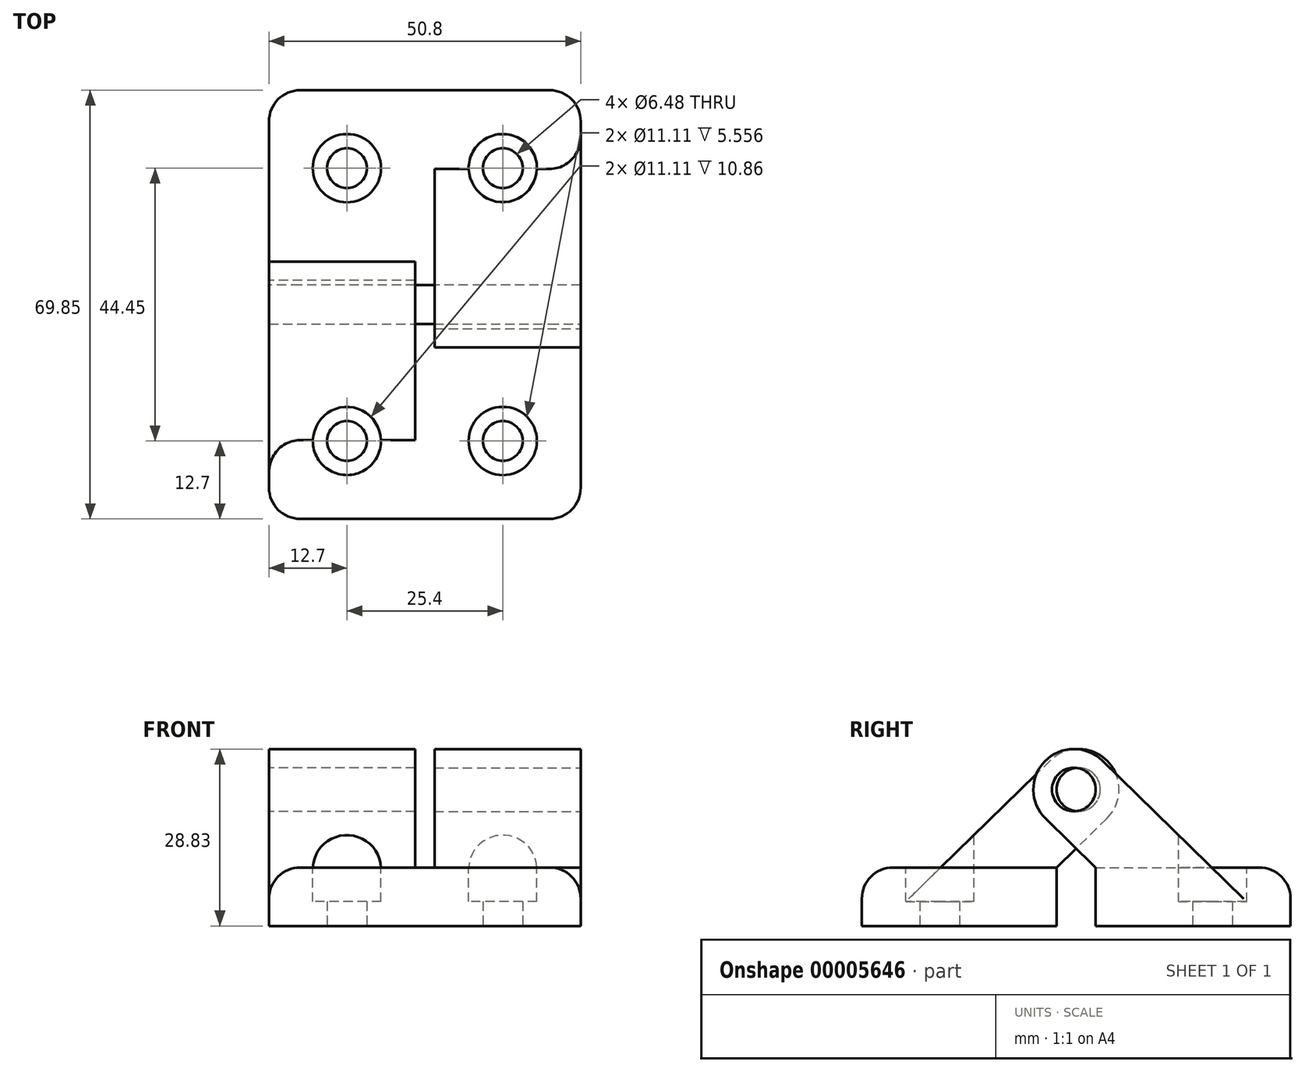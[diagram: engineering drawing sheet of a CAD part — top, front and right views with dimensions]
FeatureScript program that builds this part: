
annotation { "Feature Type Name" : "Feature", "Feature Type Description" : "" }
export const myFeature = defineFeature(function(context is Context, id is Id, definition is map)
    precondition{}
    {
        {
            var Q0;
            Q0=qCreatedBy(makeId("Top.planeOp"),FACE);
            var sketch = newSketch(context, id + "F0", { "sketchPlane" : qUnion([Q0])});
            skLineSegment(sketch, "E0.bottom", {"start": v(0, 0) * mm, "end": v(-50.8, 0) * mm});
            skLineSegment(sketch, "E0.top", {"start": v(0, 31.75) * mm, "end": v(-50.8, 31.75) * mm});
            skLineSegment(sketch, "E0.left", {"start": v(0, 0) * mm, "end": v(0, 31.75) * mm});
            skLineSegment(sketch, "E0.right", {"start": v(-50.8, 0) * mm, "end": v(-50.8, 31.75) * mm});
            skSolve(sketch);
        }
        {
            var Q0;
            Q0=makeQuery(id+"F0.imprint","IMPRINT",FACE,{"disambiguationData":[TD([[makeQuery(id+"F0.imprint","IMPRINT",EDGE,{"derivedFrom":sQuery(id+"F0.wireOp",EDGE,"E0.bottom")}),-1.0]])]});
            extrude(context, id + "F1", {"entities" : qUnion([Q0]), "depth" : 9.52 * mm});
        }
        {
            var Q0;
            Q0=makeQuery(id+"F1.opExtrude","SWEPT_FACE",FACE,{"disambiguationData":[OSD([sQuery(id+"F0.wireOp",EDGE,"E0.left")])]});
            var sketch = newSketch(context, id + "F2", { "sketchPlane" : qUnion([Q0])});
            skCircle(sketch, "E1", {"center": v(-3.56, 22.23) * mm, "radius": 3.56 * mm});
            skCircle(sketch, "E2", {"center": v(-3.56, 22.23) * mm, "radius": 6.6 * mm});
            skLineSegment(sketch, "E3", {"start": v(-8.17, 17.5) * mm, "end": v(0, 9.52) * mm});
            skLineSegment(sketch, "E4", {"start": v(1.06, 26.95) * mm, "end": v(18.9, 9.52) * mm});
            skSolve(sketch);
        }
        {
            var Q0;
            Q0 = qSketchRegion(id + "F2", true);
            var Q1;
            {var subQ3=sQuery(id+"F2.wireOp",EDGE,"E3");Q1=makeQuery(id+"F2.imprint","IMPRINT",FACE,{"disambiguationData":[TD([[makeQuery(id+"F2.imprint","IMPRINT",EDGE,{"derivedFrom":subQ3}),1.0]])]});}
            extrude(context, id + "F3", {"entities" : qUnion([Q0, Q1]), "operationType" : NewBodyOperationType.ADD, "oppositeDirection" : true, "depth" : 23.8 * mm});
        }
        {
            var Q0;
            Q0=makeQuery(id+"F1.opExtrude","CAP_FACE",FACE,{"disambiguationData":[OSD([sQuery(id+"F0.wireOp",EDGE,"E0.bottom"),sQuery(id+"F0.wireOp",EDGE,"E0.top"),sQuery(id+"F0.wireOp",EDGE,"E0.left"),sQuery(id+"F0.wireOp",EDGE,"E0.right")])],"isStart":true});
            var sketch = newSketch(context, id + "F4", { "sketchPlane" : qUnion([Q0])});
            skCircle(sketch, "E5", {"center": v(-12.7, -19.05) * mm, "radius": 3.24 * mm});
            skCircle(sketch, "E6", {"center": v(-38.1, -19.05) * mm, "radius": 3.24 * mm});
            skSolve(sketch);
        }
        {
            var Q0;
            Q0 = qSketchRegion(id + "F4", true);
            extrude(context, id + "F5", {"entities" : qUnion([Q0]), "operationType" : NewBodyOperationType.REMOVE, "oppositeDirection" : true, "depth" : 25.4 * mm});
        }
        {
            var Q0;
            Q0=makeQuery(id+"F1.opExtrude","CAP_FACE",FACE,{"disambiguationData":[OSD([sQuery(id+"F0.wireOp",EDGE,"E0.bottom"),sQuery(id+"F0.wireOp",EDGE,"E0.top"),sQuery(id+"F0.wireOp",EDGE,"E0.left"),sQuery(id+"F0.wireOp",EDGE,"E0.right")])],"isStart":false});
            var sketch = newSketch(context, id + "F6", { "sketchPlane" : qUnion([Q0])});
            skCircle(sketch, "E7.0", {"center": v(-38.1, 19.05) * mm, "radius": 3.24 * mm});
            skCircle(sketch, "E7.1", {"center": v(-12.7, 19.05) * mm, "radius": 3.24 * mm});
            skCircle(sketch, "E8", {"center": v(-38.1, 19.05) * mm, "radius": 5.56 * mm});
            skCircle(sketch, "E9", {"center": v(-12.7, 19.05) * mm, "radius": 5.56 * mm});
            skSolve(sketch);
        }
        {
            var Q0;
            Q0 = qSketchRegion(id + "F6", true);
            extrude(context, id + "F7", {"entities" : qUnion([Q0]), "operationType" : NewBodyOperationType.REMOVE, "oppositeDirection" : true, "depth" : 5.56 * mm});
        }
        {
            var Q0;
            Q0=makeQuery(id+"F6.imprint","IMPRINT",FACE,{"disambiguationData":[TD([[makeQuery(id+"F6.imprint","IMPRINT",EDGE,{"derivedFrom":sQuery(id+"F6.wireOp",EDGE,"E7.1")}),-1.0]])]});
            extrude(context, id + "F8", {"entities" : qUnion([Q0]), "operationType" : NewBodyOperationType.REMOVE, "endBound" : BoundingType.THROUGH_ALL, "depth" : 25.4 * mm});
        }
        {
            var Q0;
            Q0=makeQuery(id+"F1.opExtrude","CAP_EDGE",EDGE,{"disambiguationData":[OSD([sQuery(id+"F0.wireOp",EDGE,"E0.left")])],"isStart":false});
            var Q1;
            Q1=makeQuery(id+"F1.opExtrude","CAP_EDGE",EDGE,{"disambiguationData":[OSD([sQuery(id+"F0.wireOp",EDGE,"E0.top")])],"isStart":false});
            var Q2;
            Q2=makeQuery(id+"F1.opExtrude","CAP_EDGE",EDGE,{"disambiguationData":[OSD([sQuery(id+"F0.wireOp",EDGE,"E0.right")])],"isStart":false});
            var Q3;
            Q3=makeQuery(id+"F1.opExtrude","SWEPT_EDGE",EDGE,{"disambiguationData":[OSD([sQuery(id+"F0.wireOp",EDGE,"E0.top"),sQuery(id+"F0.wireOp",EDGE,"E0.right")])]});
            var Q4;
            Q4=makeQuery(id+"F1.opExtrude","SWEPT_EDGE",EDGE,{"disambiguationData":[OSD([sQuery(id+"F0.wireOp",EDGE,"E0.top"),sQuery(id+"F0.wireOp",EDGE,"E0.left")])]});
            fillet(context, id + "F9", {"entities" : qUnion([Q0, Q1, Q2, Q3, Q4]), "radius" : 5.08 * mm, "tangentPropagation" : true, "allowEdgeOverflow" : false});
        }
        {
            var Q0;
            Q0=makeQuery(id+"F1.opExtrude","SWEPT_BODY",BODY,{"disambiguationData":[OSD([sQuery(id+"F0.wireOp",EDGE,"E0.bottom"),sQuery(id+"F0.wireOp",EDGE,"E0.top"),sQuery(id+"F0.wireOp",EDGE,"E0.left"),sQuery(id+"F0.wireOp",EDGE,"E0.right")])]});
            var Q1;
            Q1=makeQuery(id+"F1.opExtrude","SWEPT_EDGE",EDGE,{"disambiguationData":[OSD([sQuery(id+"F0.wireOp",EDGE,"E0.bottom"),sQuery(id+"F0.wireOp",EDGE,"E0.left")])]});
            transform(context, id + "F10", {"entities" : qUnion([Q0]), "transformType" : TransformType.ROTATION, "transformAxis" : qUnion([Q1]), "angle" : 180 * degree, "makeCopy" : true});
        }
        {
            var Q0;
            Q0=makeQuery(id+"F10.opPattern","COPY",BODY,{"derivedFrom":makeQuery(id+"F1.opExtrude","SWEPT_BODY",BODY,{"disambiguationData":[OSD([sQuery(id+"F0.wireOp",EDGE,"E0.bottom"),sQuery(id+"F0.wireOp",EDGE,"E0.top"),sQuery(id+"F0.wireOp",EDGE,"E0.left"),sQuery(id+"F0.wireOp",EDGE,"E0.right")])]}),"instanceName":"1"});
            transform(context, id + "F11", {"entities" : qUnion([Q0]), "transformType" : TransformType.TRANSLATION_3D, "dx" : -50.8 * mm, "dy" : 0 * mm, "dz" : 0 * mm, "makeCopy" : false});
        }
        {
            var Q0;
            Q0=makeQuery(id+"F10.opPattern","COPY",BODY,{"derivedFrom":makeQuery(id+"F1.opExtrude","SWEPT_BODY",BODY,{"disambiguationData":[OSD([sQuery(id+"F0.wireOp",EDGE,"E0.bottom"),sQuery(id+"F0.wireOp",EDGE,"E0.top"),sQuery(id+"F0.wireOp",EDGE,"E0.left"),sQuery(id+"F0.wireOp",EDGE,"E0.right")])]}),"instanceName":"1"});
            transform(context, id + "F12", {"entities" : qUnion([Q0]), "transformType" : TransformType.TRANSLATION_3D, "dx" : 0 * mm, "dy" : -6.35 * mm, "dz" : 0 * mm, "makeCopy" : false});
        }
    });
